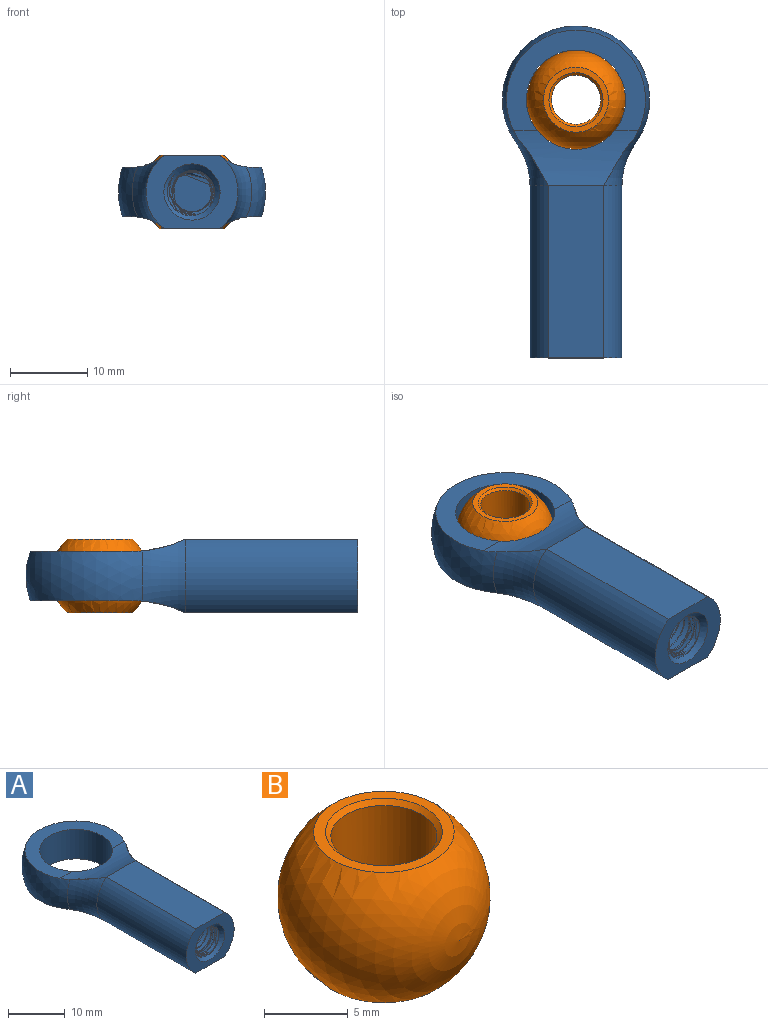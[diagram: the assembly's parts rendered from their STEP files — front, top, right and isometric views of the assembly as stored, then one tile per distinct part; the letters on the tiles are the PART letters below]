
ASSEMBLY  parts=2 mates=1
PART A: 19 faces, bbox 19.7x43.6x19.7 mm
  f0: torus R=15.47mm, axis (0,-1,0), area 52.1mm2, adj f2,f13,f16,f17
  f1: plane 11.89x9.53mm, normal (0,-1,0), area 58.2mm2, adj f2,f3,f4,f10,f11
  f2: cylinder r=5.94mm len=22.22mm, axis (0,1,0), area 245.5mm2, adj f0,f1,f10,f11
  f3: cylinder r=5.94mm len=22.22mm, axis (0,1,0), area 245.5mm2, adj f1,f10,f11,f12
  f4: cone r=3.63mm half-angle=45deg, axis (0,-1,0), area 21.4mm2, adj f1,f6,f7,f8,f9
  f5: plane 6.15x6.13mm, normal (0,-1,0), area 26.2mm2, adj f6,f7,f8,f9
  f6: bspline ~17.35x6.35mm, area 227.2mm2, adj f4,f5,f7,f9
  f7: bspline ~16.78x5.17mm, area 33.3mm2, adj f4,f5,f6,f8
  f8: bspline ~17.91x6.35mm, area 226.8mm2, adj f4,f5,f7,f9
  f9: cylinder r=3.17mm len=17.01mm, axis (0,-1,0), area 30.2mm2, adj f4,f5,f6,f8
  f10: plane 22.22x7.11mm, normal (0,0,1), area 158mm2, adj f1,f2,f3,f16
  f11: plane 22.22x7.11mm, normal (0,0,-1), area 158mm2, adj f1,f2,f3,f17
  f12: torus R=15.47mm, axis (0,-1,0), area 52.1mm2, adj f3,f13,f16,f17
  f13: sphere r=9.53mm, area 269.5mm2, adj f0,f12,f14,f15,f16,f17
  f14: plane 17.96x13mm, normal (0,0,1), area 83.8mm2, adj f13,f16,f18
  f15: plane 18.66x13.7mm, normal (0,0,-1), area 83.8mm2, adj f13,f17,f18
  f16: cylinder r=16.67mm len=16.06mm, axis (-1,0,0), area 67.8mm2, adj f0,f10,f12,f13,f14,f18
  f17: cylinder r=16.67mm len=16.06mm, axis (1,0,0), area 67.8mm2, adj f0,f11,f12,f13,f15,f18
  f18: cylinder r=6.41mm len=12.83mm, axis (0,0,1), area 255.9mm2, adj f14,f15,f16,f17
PART B: 6 faces, bbox 12.7x12.7x12.7 mm
  f0: sphere r=6.35mm, area 380mm2, adj f1,f2
  f1: plane 8.4x8.4mm, normal (0,0,1), area 17.1mm2, adj f0,f5
  f2: plane 8.4x8.4mm, normal (0,0,-1), area 17.1mm2, adj f0,f4
  f3: cylinder r=3.17mm len=8.89mm, axis (0,0,1), area 177.3mm2, adj f4,f5
  f4: cone r=3.49mm half-angle=45deg, axis (0,0,-1), area 9.4mm2, adj f2,f3
  f5: cone r=3.49mm half-angle=45deg, axis (0,0,1), area 9.4mm2, adj f1,f3
PLACE A at identity
PLACE B at identity
MATE ball B.f3 <-> A.f18  axis (0,0,1) through (0,15.88,0)mm
